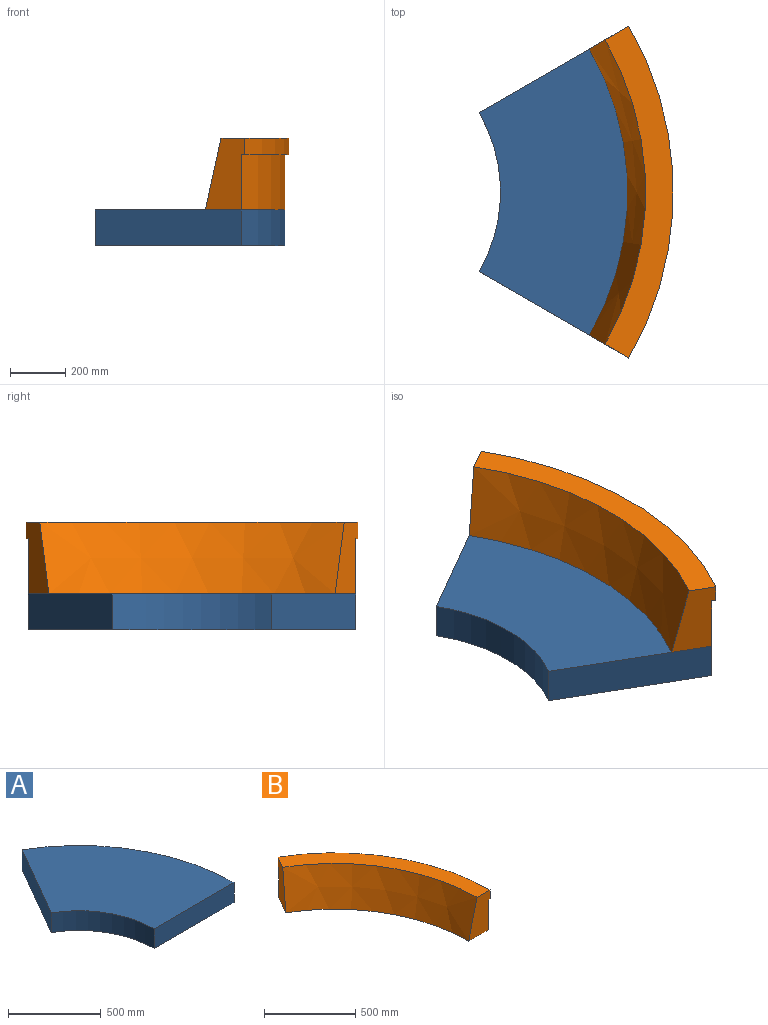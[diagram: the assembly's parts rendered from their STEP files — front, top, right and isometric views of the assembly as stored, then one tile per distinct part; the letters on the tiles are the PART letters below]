
ASSEMBLY  parts=2 mates=1
PART A: 6 faces, bbox 897.5x1026.2x130 mm
  f0: plane 1026.24x897.5mm, normal (0,0,1), area 562135.6mm2, adj f1,f3,f4,f5
  f1: cylinder r=575mm len=497.96mm, axis (0,0,-1), area 78278mm2, adj f0,f2,f4,f5
  f2: plane 1026.24x897.5mm, normal (0,0,-1), area 562135.6mm2, adj f1,f3,f4,f5
  f3: cylinder r=1185mm len=1026.24mm, axis (0,0,-1), area 161320.8mm2, adj f0,f2,f4,f5
  f4: plane 528.28x305mm, normal (-0.87,0.5,0), area 79300mm2, adj f0,f1,f2,f3
  f5: plane 610x130mm, normal (0,-1,0), area 79300mm2, adj f0,f1,f2,f3
PART B: 8 faces, bbox 682.5x1039.2x260 mm
  f0: cone r=1035mm half-angle=14deg, axis (0,0,1), area 299594.8mm2, adj f1,f5,f6,f7
  f1: plane 1026.24x667.5mm, normal (0,0,-1), area 174358.4mm2, adj f0,f2,f6,f7
  f2: cylinder r=1185mm len=1026.24mm, axis (0,0,-1), area 248185.8mm2, adj f1,f3,f6,f7
  f3: plane 1039.23x607.5mm, normal (0,0,-1), area 18731.7mm2, adj f2,f4,f6,f7
  f4: cylinder r=1200mm len=1039.23mm, axis (0,0,-1), area 75398.2mm2, adj f3,f5,f6,f7
  f5: plane 1039.23x650mm, normal (0,0,1), area 120427.7mm2, adj f0,f4,f6,f7
  f6: plane 260x142.89mm, normal (-0.87,0.5,0), area 31450mm2, adj f0,f1,f2,f3,f4,f5
  f7: plane 260x165mm, normal (0,-1,0), area 31450mm2, adj f0,f1,f2,f3,f4,f5
PLACE A rot(axis=(0,0,-1),30deg) t=(-170.72,267.91,-244.04)mm
PLACE B rot(axis=(0,0,-1),30deg) t=(-170.72,267.91,-114.04)mm
MATE fastened B.f6 <-> A.f4  axis (-0.5,0.87,0) through (855.52,860.41,-114.04)mm
